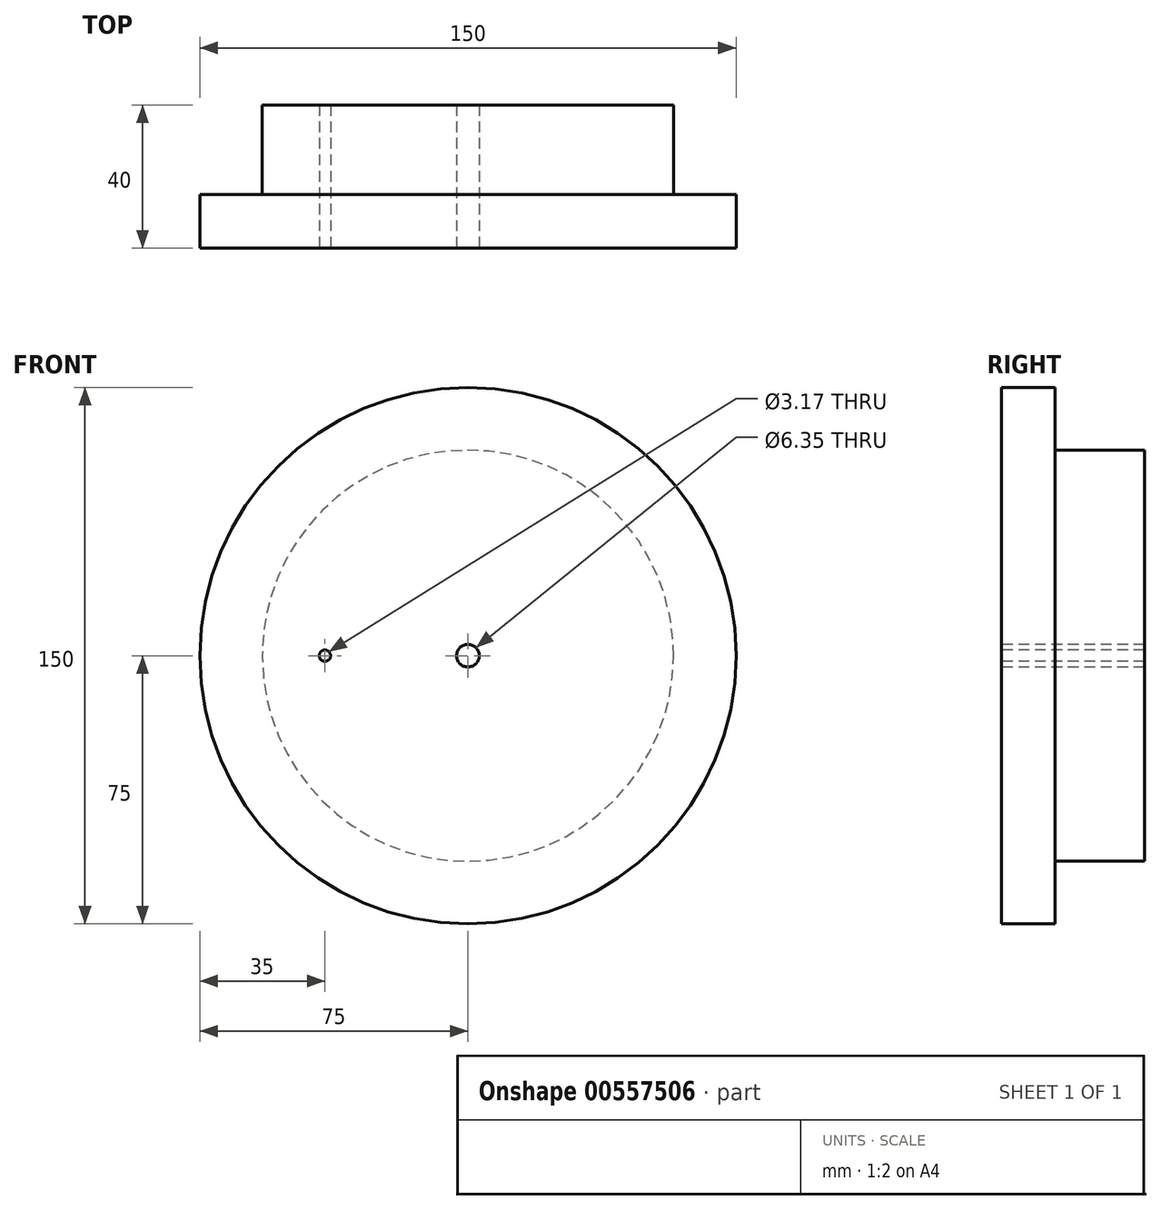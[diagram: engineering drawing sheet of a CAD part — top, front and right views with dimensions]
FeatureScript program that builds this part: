
annotation { "Feature Type Name" : "Feature", "Feature Type Description" : "" }
export const myFeature = defineFeature(function(context is Context, id is Id, definition is map)
    precondition{}
    {
        {
            var Q0;
            Q0=qCreatedBy(makeId("Front.planeOp"),FACE);
            var sketch = newSketch(context, id + "F0", { "sketchPlane" : qUnion([Q0])});
            skCircle(sketch, "E0", {"center": v(0, 0) * mm, "radius": 75 * mm});
            skSolve(sketch);
        }
        {
            var Q0;
            Q0 = qSketchRegion(id + "F0", true);
            extrude(context, id + "F1", {"entities" : qUnion([Q0]), "depth" : 15 * mm, "offsetDistance" : 25 * mm});
        }
        {
            var Q0;
            Q0=makeQuery(id+"F1.opExtrude","CAP_FACE",FACE,{"disambiguationData":[OSD([sQuery(id+"F0.wireOp",EDGE,"E0")])],"isStart":true});
            var sketch = newSketch(context, id + "F2", { "sketchPlane" : qUnion([Q0])});
            skCircle(sketch, "E1", {"center": v(0, 0) * mm, "radius": 57.5 * mm});
            skSolve(sketch);
        }
        {
            var Q0;
            Q0 = qSketchRegion(id + "F2", true);
            extrude(context, id + "F3", {"entities" : qUnion([Q0]), "operationType" : NewBodyOperationType.ADD, "depth" : 25 * mm, "offsetDistance" : 25 * mm});
        }
        {
            var Q0;
            Q0=makeQuery(id+"F1.opExtrude","CAP_FACE",FACE,{"disambiguationData":[OSD([sQuery(id+"F0.wireOp",EDGE,"E0")])],"isStart":false});
            var sketch = newSketch(context, id + "F4", { "sketchPlane" : qUnion([Q0])});
            skCircle(sketch, "E2", {"center": v(0, 0) * mm, "radius": 3.18 * mm});
            skCircle(sketch, "E3", {"center": v(-40, 0) * mm, "radius": 1.59 * mm});
            skSolve(sketch);
        }
        {
            var Q0;
            Q0 = qSketchRegion(id + "F4", true);
            extrude(context, id + "F5", {"entities" : qUnion([Q0]), "operationType" : NewBodyOperationType.REMOVE, "endBound" : BoundingType.THROUGH_ALL, "oppositeDirection" : true, "depth" : 25 * mm, "offsetDistance" : 25 * mm});
        }
    });
